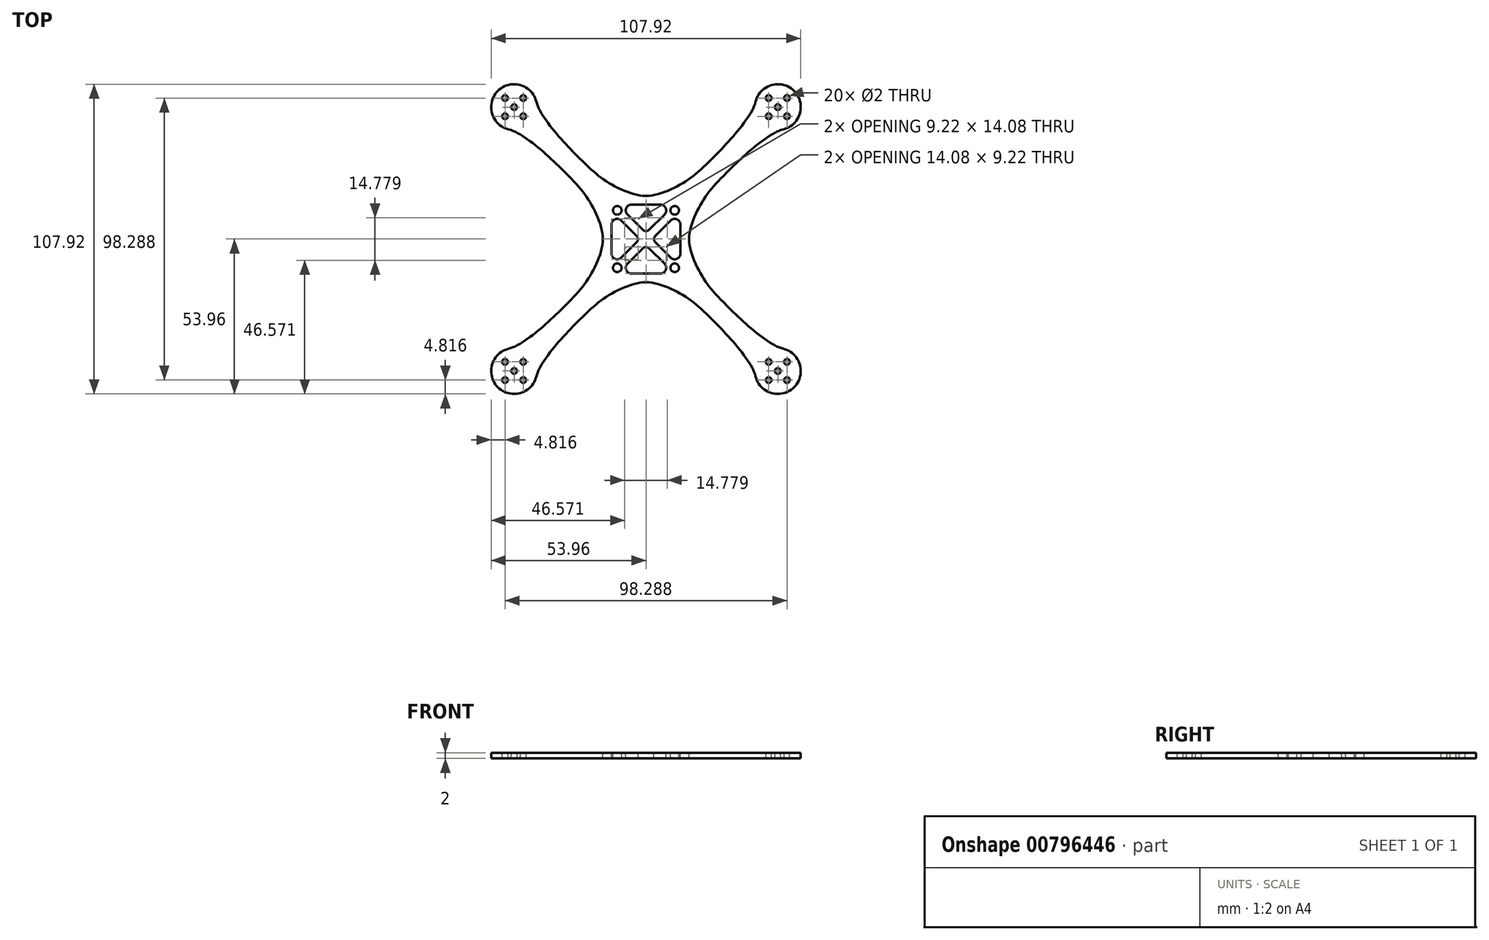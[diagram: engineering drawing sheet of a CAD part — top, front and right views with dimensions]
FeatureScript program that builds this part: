
annotation { "Feature Type Name" : "Feature", "Feature Type Description" : "" }
export const myFeature = defineFeature(function(context is Context, id is Id, definition is map)
    precondition{}
    {
        {
            var Q0;
            Q0=qCreatedBy(makeId("Top.planeOp"),FACE);
            var sketch = newSketch(context, id + "F0", { "sketchPlane" : qUnion([Q0])});
            skCircle(sketch, "E0", {"center": v(0, 0) * mm, "radius": 65 * mm, "construction": true});
            skLineSegment(sketch, "E1", {"start": v(0, 0) * mm, "end": v(-45.96, 45.96) * mm, "construction": true});
            skCircle(sketch, "E2", {"center": v(-45.96, 45.96) * mm, "radius": 4.5 * mm, "construction": true});
            skPoint(sketch, "E3", {"position": v(-42.78, 42.78) * mm});
            skLineSegment(sketch, "E4.bottom", {"start": v(-42.78, 42.78) * mm, "end": v(-49.14, 42.78) * mm, "construction": true});
            skLineSegment(sketch, "E4.top", {"start": v(-42.78, 49.14) * mm, "end": v(-49.14, 49.14) * mm, "construction": true});
            skLineSegment(sketch, "E4.left", {"start": v(-42.78, 42.78) * mm, "end": v(-42.78, 49.14) * mm, "construction": true});
            skLineSegment(sketch, "E4.right", {"start": v(-49.14, 42.78) * mm, "end": v(-49.14, 49.14) * mm, "construction": true});
            skPoint(sketch, "E5", {"position": v(-49.14, 42.78) * mm});
            skPoint(sketch, "E6", {"position": v(-49.14, 49.14) * mm});
            skPoint(sketch, "E7", {"position": v(-42.78, 49.14) * mm});
            skArc(sketch, "E8", {"start": v(-38.4, 43.35) * mm, "mid": v(-51.62, 51.62) * mm, "end": v(-43.35, 38.4) * mm});
            skLineSegment(sketch, "E9", {"start": v(-15, 10.05) * mm, "end": v(-43.35, 38.4) * mm});
            skLineSegment(sketch, "E10", {"start": v(-38.4, 43.35) * mm, "end": v(-10.05, 15) * mm});
            skLineSegment(sketch, "E11.bottom", {"start": v(-10.05, 15) * mm, "end": v(0, 15) * mm});
            skLineSegment(sketch, "E11.left", {"start": v(-15, 10.05) * mm, "end": v(-15, 0) * mm});
            skLineSegment(sketch, "E12", {"start": v(-15, 0) * mm, "end": v(0, 0) * mm});
            skLineSegment(sketch, "E13", {"start": v(0, 15) * mm, "end": v(0, 0) * mm});
            skPoint(sketch, "E11.right.start.orphan", {"position": v(15, 15) * mm});
            skPoint(sketch, "E11.top.end.orphan", {"position": v(15, -15) * mm});
            skPoint(sketch, "E14.orphan", {"position": v(-15, -15) * mm});
            skPoint(sketch, "E15.orphan", {"position": v(-4.95, 0) * mm});
            skPoint(sketch, "E16.orphan", {"position": v(0, 4.95) * mm});
            skPoint(sketch, "E17.orphan", {"position": v(-15, 15) * mm});
            skFitSpline(sketch, "E18", {"points": [v(-47.78, 38.17) * mm, v(-28.1, 23.15) * mm, v(-19.07, 12.07) * mm, v(-15, 0) * mm], "startDerivative": vector(38.91, -9.08) * mm, "endDerivative": vector(0, -38.08) * mm});
            skLineSegment(sketch, "E19", {"start": v(-15, 0) * mm, "end": v(-15, -15) * mm, "construction": true});
            skFitSpline(sketch, "E20.MirrorCS", {"points": [v(-38.17, 47.78) * mm, v(-23.15, 28.1) * mm, v(-12.07, 19.07) * mm, v(0, 15) * mm], "startDerivative": vector(9.08, -38.91) * mm, "endDerivative": vector(38.08, 0) * mm});
            skSolve(sketch);
        }
        {
            var Q0;
            Q0=makeQuery(id+"F0.imprint","IMPRINT",FACE,{"disambiguationData":[TD([[makeQuery(id+"F0.imprint","IMPRINT",EDGE,{"derivedFrom":sQuery(id+"F0.wireOp",EDGE,"E8")}),1.0]])]});
            var Q1;
            {var subQ0=sQuery(id+"F0.wireOp",EDGE,"E10");var subQ1=sQuery(id+"F0.wireOp",EDGE,"E8");var subQ2=makeQuery(id+"F0.imprint","INTERSECT",VERTEX,{"derivedFrom":[subQ1,subQ0]});Q1=makeQuery(id+"F0.imprint","IMPRINT",FACE,{"disambiguationData":[TD([[makeQuery(id+"F0.imprint","IMPRINT",EDGE,{"disambiguationData":[TD([[subQ2,-1.0]])],"derivedFrom":subQ1}),-1.0]])]});}
            var Q2;
            {var subQ0=sQuery(id+"F0.wireOp",EDGE,"E9");var subQ1=sQuery(id+"F0.wireOp",EDGE,"E8");var subQ2=makeQuery(id+"F0.imprint","INTERSECT",VERTEX,{"derivedFrom":[subQ1,subQ0]});Q2=makeQuery(id+"F0.imprint","IMPRINT",FACE,{"disambiguationData":[TD([[makeQuery(id+"F0.imprint","IMPRINT",EDGE,{"disambiguationData":[TD([[subQ2,1.0]])],"derivedFrom":subQ1}),-1.0]])]});}
            var Q3;
            {var subQ0=sQuery(id+"F0.wireOp",EDGE,"E11.left");Q3=makeQuery(id+"F0.imprint","IMPRINT",FACE,{"disambiguationData":[TD([[makeQuery(id+"F0.imprint","IMPRINT",EDGE,{"derivedFrom":subQ0}),-1.0]])]});}
            var Q4;
            {var subQ0=sQuery(id+"F0.wireOp",EDGE,"E11.bottom");Q4=makeQuery(id+"F0.imprint","IMPRINT",FACE,{"disambiguationData":[TD([[makeQuery(id+"F0.imprint","IMPRINT",EDGE,{"derivedFrom":subQ0}),1.0]])]});}
            extrude(context, id + "F1", {"entities" : qUnion([Q0, Q1, Q2, Q3, Q4]), "oppositeDirection" : true, "depth" : 2 * mm, "offsetDistance" : 25 * mm});
        }
        {
            var Q0;
            Q0=sQuery(id+"F0.wireOp",VERTEX,"E4.bottom.end");
            var Q1;
            Q1=sQuery(id+"F0.wireOp",VERTEX,"E3");
            var Q2;
            Q2=sQuery(id+"F0.wireOp",VERTEX,"E7");
            var Q3;
            Q3=sQuery(id+"F0.wireOp",VERTEX,"E6");
            var Q4;
            Q4=sQuery(id+"F0.wireOp",VERTEX,"E2.center");
            var Q5;
            Q5=makeQuery(id+"F1.opExtrude","SWEPT_BODY",BODY,{"disambiguationData":[OSD([sQuery(id+"F0.wireOp",EDGE,"E8"),sQuery(id+"F0.wireOp",EDGE,"E9"),sQuery(id+"F0.wireOp",EDGE,"E10"),sQuery(id+"F0.wireOp",EDGE,"E11.bottom"),sQuery(id+"F0.wireOp",EDGE,"E11.left"),sQuery(id+"F0.wireOp",EDGE,"E12"),sQuery(id+"F0.wireOp",EDGE,"E13")])]});
            hole(context, id + "F2", {"style" : HoleStyle.SIMPLE, "endStyle" : HoleEndStyle.BLIND, "holeDiameter" : 2 * mm, "majorDiameter" : 5 * mm, "holeDepth" : 5 * mm, "isTappedThrough" : true, "tappedDepth" : 12 * mm, "tapClearance" : 3, "locations" : qUnion([Q0, Q1, Q2, Q3, Q4]), "scope" : qUnion([Q5])});
        }
        {
            var Q0;
            Q0=makeQuery(id+"F1.opExtrude","SWEPT_BODY",BODY,{"disambiguationData":[OSD([sQuery(id+"F0.wireOp",EDGE,"E8"),sQuery(id+"F0.wireOp",EDGE,"E9"),sQuery(id+"F0.wireOp",EDGE,"E10"),sQuery(id+"F0.wireOp",EDGE,"E11.bottom"),sQuery(id+"F0.wireOp",EDGE,"E11.left"),sQuery(id+"F0.wireOp",EDGE,"E12"),sQuery(id+"F0.wireOp",EDGE,"E13")])]});
            var Q1;
            Q1=makeQuery(id+"F1.opExtrude","SWEPT_FACE",FACE,{"disambiguationData":[OSD([sQuery(id+"F0.wireOp",EDGE,"E13")])]});
            mirror(context, id + "F3", {"operationType" : NewBodyOperationType.ADD, "entities" : qUnion([Q0]), "mirrorPlane" : qUnion([Q1])});
        }
        {
            var Q0;
            Q0=makeQuery(id+"F1.opExtrude","SWEPT_BODY",BODY,{"disambiguationData":[OSD([sQuery(id+"F0.wireOp",EDGE,"E8"),sQuery(id+"F0.wireOp",EDGE,"E9"),sQuery(id+"F0.wireOp",EDGE,"E10"),sQuery(id+"F0.wireOp",EDGE,"E11.bottom"),sQuery(id+"F0.wireOp",EDGE,"E11.left"),sQuery(id+"F0.wireOp",EDGE,"E12"),sQuery(id+"F0.wireOp",EDGE,"E13")])]});
            var Q1;
            {var subQ0=makeQuery(id+"F1.opExtrude","SWEPT_FACE",FACE,{"disambiguationData":[OSD([sQuery(id+"F0.wireOp",EDGE,"E12")])]});Q1=makeQuery(id+"F3.boolean.opBoolean","MERGE",FACE,{"derivedFrom":[subQ0,makeQuery(id+"F3.opPattern","COPY",FACE,{"derivedFrom":subQ0,"instanceName":"1"})]});}
            mirror(context, id + "F4", {"operationType" : NewBodyOperationType.ADD, "entities" : qUnion([Q0]), "mirrorPlane" : qUnion([Q1])});
        }
        {
            var Q0;
            {var subQ0=makeQuery(id+"F1.opExtrude","CAP_FACE",FACE,{"disambiguationData":[OSD([sQuery(id+"F0.wireOp",EDGE,"E8"),sQuery(id+"F0.wireOp",EDGE,"E9"),sQuery(id+"F0.wireOp",EDGE,"E10"),sQuery(id+"F0.wireOp",EDGE,"E11.bottom"),sQuery(id+"F0.wireOp",EDGE,"E11.left"),sQuery(id+"F0.wireOp",EDGE,"E12"),sQuery(id+"F0.wireOp",EDGE,"E13")])],"isStart":true});var subQ1=makeQuery(id+"F3.boolean.opBoolean","MERGE",FACE,{"derivedFrom":[subQ0,makeQuery(id+"F3.opPattern","COPY",FACE,{"derivedFrom":subQ0,"instanceName":"1"})]});Q0=makeQuery(id+"F4.boolean.opBoolean","MERGE",FACE,{"derivedFrom":[subQ1,makeQuery(id+"F4.opPattern","COPY",FACE,{"derivedFrom":subQ1,"instanceName":"1"})]});}
            var sketch = newSketch(context, id + "F5", { "sketchPlane" : qUnion([Q0])});
            skLineSegment(sketch, "E21.bottom", {"start": v(-10, 10) * mm, "end": v(10, 10) * mm, "construction": true});
            skLineSegment(sketch, "E21.top", {"start": v(-10, -10) * mm, "end": v(10, -10) * mm, "construction": true});
            skLineSegment(sketch, "E21.left", {"start": v(-10, 10) * mm, "end": v(-10, -10) * mm, "construction": true});
            skLineSegment(sketch, "E21.right", {"start": v(10, 10) * mm, "end": v(10, -10) * mm, "construction": true});
            skPoint(sketch, "E21.middle", {"position": v(0, 0) * mm});
            skPoint(sketch, "E22", {"position": v(-10, 10) * mm});
            skPoint(sketch, "E23", {"position": v(10, 10) * mm});
            skPoint(sketch, "E24", {"position": v(10, -10) * mm});
            skPoint(sketch, "E25", {"position": v(-10, -10) * mm});
            skSolve(sketch);
        }
        {
            var Q0;
            Q0=sQuery(id+"F5.wireOp",VERTEX,"E22");
            var Q1;
            Q1=sQuery(id+"F5.wireOp",VERTEX,"E23");
            var Q2;
            Q2=sQuery(id+"F5.wireOp",VERTEX,"E24");
            var Q3;
            Q3=sQuery(id+"F5.wireOp",VERTEX,"E25");
            var Q4;
            Q4=makeQuery(id+"F1.opExtrude","SWEPT_BODY",BODY,{"disambiguationData":[OSD([sQuery(id+"F0.wireOp",EDGE,"E8"),sQuery(id+"F0.wireOp",EDGE,"E9"),sQuery(id+"F0.wireOp",EDGE,"E10"),sQuery(id+"F0.wireOp",EDGE,"E11.bottom"),sQuery(id+"F0.wireOp",EDGE,"E11.left"),sQuery(id+"F0.wireOp",EDGE,"E12"),sQuery(id+"F0.wireOp",EDGE,"E13")])]});
            hole(context, id + "F6", {"style" : HoleStyle.SIMPLE, "endStyle" : HoleEndStyle.BLIND, "holeDiameter" : 3 * mm, "majorDiameter" : 5 * mm, "holeDepth" : 5 * mm, "isTappedThrough" : true, "tappedDepth" : 12 * mm, "tapClearance" : 3, "locations" : qUnion([Q0, Q1, Q2, Q3]), "scope" : qUnion([Q4])});
        }
        {
            var Q0;
            {var subQ0=makeQuery(id+"F1.opExtrude","CAP_FACE",FACE,{"disambiguationData":[OSD([sQuery(id+"F0.wireOp",EDGE,"E8"),sQuery(id+"F0.wireOp",EDGE,"E9"),sQuery(id+"F0.wireOp",EDGE,"E10"),sQuery(id+"F0.wireOp",EDGE,"E11.bottom"),sQuery(id+"F0.wireOp",EDGE,"E11.left"),sQuery(id+"F0.wireOp",EDGE,"E12"),sQuery(id+"F0.wireOp",EDGE,"E13")])],"isStart":true});var subQ1=makeQuery(id+"F3.boolean.opBoolean","MERGE",FACE,{"derivedFrom":[subQ0,makeQuery(id+"F3.opPattern","COPY",FACE,{"derivedFrom":subQ0,"instanceName":"1"})]});Q0=makeQuery(id+"F4.boolean.opBoolean","MERGE",FACE,{"derivedFrom":[subQ1,makeQuery(id+"F4.opPattern","COPY",FACE,{"derivedFrom":subQ1,"instanceName":"1"})]});}
            var sketch = newSketch(context, id + "F7", { "sketchPlane" : qUnion([Q0])});
            skLineSegment(sketch, "E26", {"start": v(-8.59, 6.46) * mm, "end": v(-3.24, 1.12) * mm});
            skLineSegment(sketch, "E27", {"start": v(-12, 0) * mm, "end": v(-12, 5.05) * mm});
            skPoint(sketch, "E28.visualSharp", {"position": v(-12, 9.88) * mm});
            skArc(sketch, "E28.filletArc", {"start": v(-8.59, 6.46) * mm, "mid": v(-10.77, 6.9) * mm, "end": v(-12, 5.05) * mm});
            skArc(sketch, "E29.MirrorCS", {"start": v(-8.59, -6.46) * mm, "mid": v(-10.77, -6.9) * mm, "end": v(-12, -5.05) * mm});
            skLineSegment(sketch, "E30.MirrorCS", {"start": v(-8.59, -6.46) * mm, "end": v(-3.24, -1.12) * mm});
            skLineSegment(sketch, "E31.MirrorCS", {"start": v(-12, 0) * mm, "end": v(-12, -5.05) * mm});
            skLineSegment(sketch, "E32.MirrorCS", {"start": v(-6.46, 8.59) * mm, "end": v(0, 2.12) * mm});
            skLineSegment(sketch, "E33.MirrorCS", {"start": v(0, 12) * mm, "end": v(-5.05, 12) * mm});
            skArc(sketch, "E34.MirrorCS", {"start": v(-6.46, 8.59) * mm, "mid": v(-6.9, 10.77) * mm, "end": v(-5.05, 12) * mm});
            skLineSegment(sketch, "E35.MirrorCS", {"start": v(6.46, 8.59) * mm, "end": v(1.12, 3.24) * mm});
            skLineSegment(sketch, "E36.MirrorCS", {"start": v(0, 12) * mm, "end": v(5.05, 12) * mm});
            skArc(sketch, "E37.MirrorCS", {"start": v(6.46, 8.59) * mm, "mid": v(6.9, 10.77) * mm, "end": v(5.05, 12) * mm});
            skPoint(sketch, "E38.MirrorP", {"position": v(-9.88, 12) * mm});
            skLineSegment(sketch, "E39.MirrorCS", {"start": v(6.46, 8.59) * mm, "end": v(0, 2.12) * mm});
            skLineSegment(sketch, "E40.MirrorCS", {"start": v(-6.46, 8.59) * mm, "end": v(-1.12, 3.24) * mm});
            skLineSegment(sketch, "E41", {"start": v(-10, -10) * mm, "end": v(10, 10) * mm, "construction": true});
            skArc(sketch, "E42.MirrorCS", {"start": v(8.59, 6.46) * mm, "mid": v(10.77, 6.9) * mm, "end": v(12, 5.05) * mm});
            skArc(sketch, "E43.MirrorCS", {"start": v(8.59, -6.46) * mm, "mid": v(10.77, -6.9) * mm, "end": v(12, -5.05) * mm});
            skLineSegment(sketch, "E44.MirrorCS", {"start": v(12, 0) * mm, "end": v(12, 5.05) * mm});
            skLineSegment(sketch, "E45.MirrorCS", {"start": v(12, 0) * mm, "end": v(12, -5.05) * mm});
            skPoint(sketch, "E46.MirrorP", {"position": v(12, -9.88) * mm});
            skLineSegment(sketch, "E47.MirrorCS", {"start": v(8.59, -6.46) * mm, "end": v(3.24, -1.12) * mm});
            skLineSegment(sketch, "E48.MirrorCS", {"start": v(8.59, 6.46) * mm, "end": v(3.24, 1.12) * mm});
            skLineSegment(sketch, "E49.MirrorCS", {"start": v(6.46, -8.59) * mm, "end": v(1.12, -3.24) * mm});
            skLineSegment(sketch, "E50.MirrorCS", {"start": v(-6.46, -8.59) * mm, "end": v(-1.12, -3.24) * mm});
            skArc(sketch, "E51.MirrorCS", {"start": v(-6.46, -8.59) * mm, "mid": v(-6.9, -10.77) * mm, "end": v(-5.05, -12) * mm});
            skLineSegment(sketch, "E52.MirrorCS", {"start": v(0, -12) * mm, "end": v(-5.05, -12) * mm});
            skLineSegment(sketch, "E53.MirrorCS", {"start": v(0, -12) * mm, "end": v(5.05, -12) * mm});
            skArc(sketch, "E54.MirrorCS", {"start": v(6.46, -8.59) * mm, "mid": v(6.9, -10.77) * mm, "end": v(5.05, -12) * mm});
            skPoint(sketch, "E55.visualSharp", {"position": v(-2.12, 0) * mm});
            skArc(sketch, "E55.filletArc", {"start": v(-3.24, -1.12) * mm, "mid": v(-2.78, 0) * mm, "end": v(-3.24, 1.12) * mm});
            skPoint(sketch, "E56.visualSharp", {"position": v(0, 2.12) * mm});
            skArc(sketch, "E56.filletArc", {"start": v(-1.12, 3.24) * mm, "mid": v(0, 2.78) * mm, "end": v(1.12, 3.24) * mm});
            skPoint(sketch, "E57.visualSharp", {"position": v(2.12, 0) * mm});
            skArc(sketch, "E57.filletArc", {"start": v(3.24, 1.12) * mm, "mid": v(2.78, 0) * mm, "end": v(3.24, -1.12) * mm});
            skPoint(sketch, "E58.visualSharp", {"position": v(0, -2.12) * mm});
            skArc(sketch, "E58.filletArc", {"start": v(1.12, -3.24) * mm, "mid": v(0, -2.78) * mm, "end": v(-1.12, -3.24) * mm});
            skSolve(sketch);
        }
        {
            var Q0;
            Q0=makeQuery(id+"F7.imprint","IMPRINT",FACE,{"disambiguationData":[TD([[makeQuery(id+"F7.imprint","IMPRINT",EDGE,{"derivedFrom":sQuery(id+"F7.wireOp",EDGE,"E36.MirrorCS")}),-1.0]])]});
            var Q1;
            Q1=makeQuery(id+"F7.imprint","IMPRINT",FACE,{"disambiguationData":[TD([[makeQuery(id+"F7.imprint","IMPRINT",EDGE,{"derivedFrom":sQuery(id+"F7.wireOp",EDGE,"E44.MirrorCS")}),1.0]])]});
            var Q2;
            Q2=makeQuery(id+"F7.imprint","IMPRINT",FACE,{"disambiguationData":[TD([[makeQuery(id+"F7.imprint","IMPRINT",EDGE,{"derivedFrom":sQuery(id+"F7.wireOp",EDGE,"E49.MirrorCS")}),1.0]])]});
            var Q3;
            Q3=makeQuery(id+"F7.imprint","IMPRINT",FACE,{"disambiguationData":[TD([[makeQuery(id+"F7.imprint","IMPRINT",EDGE,{"derivedFrom":sQuery(id+"F7.wireOp",EDGE,"E26")}),-1.0]])]});
            extrude(context, id + "F8", {"entities" : qUnion([Q0, Q1, Q2, Q3]), "operationType" : NewBodyOperationType.REMOVE, "oppositeDirection" : true, "depth" : 25 * mm, "offsetDistance" : 25 * mm});
        }
    });
